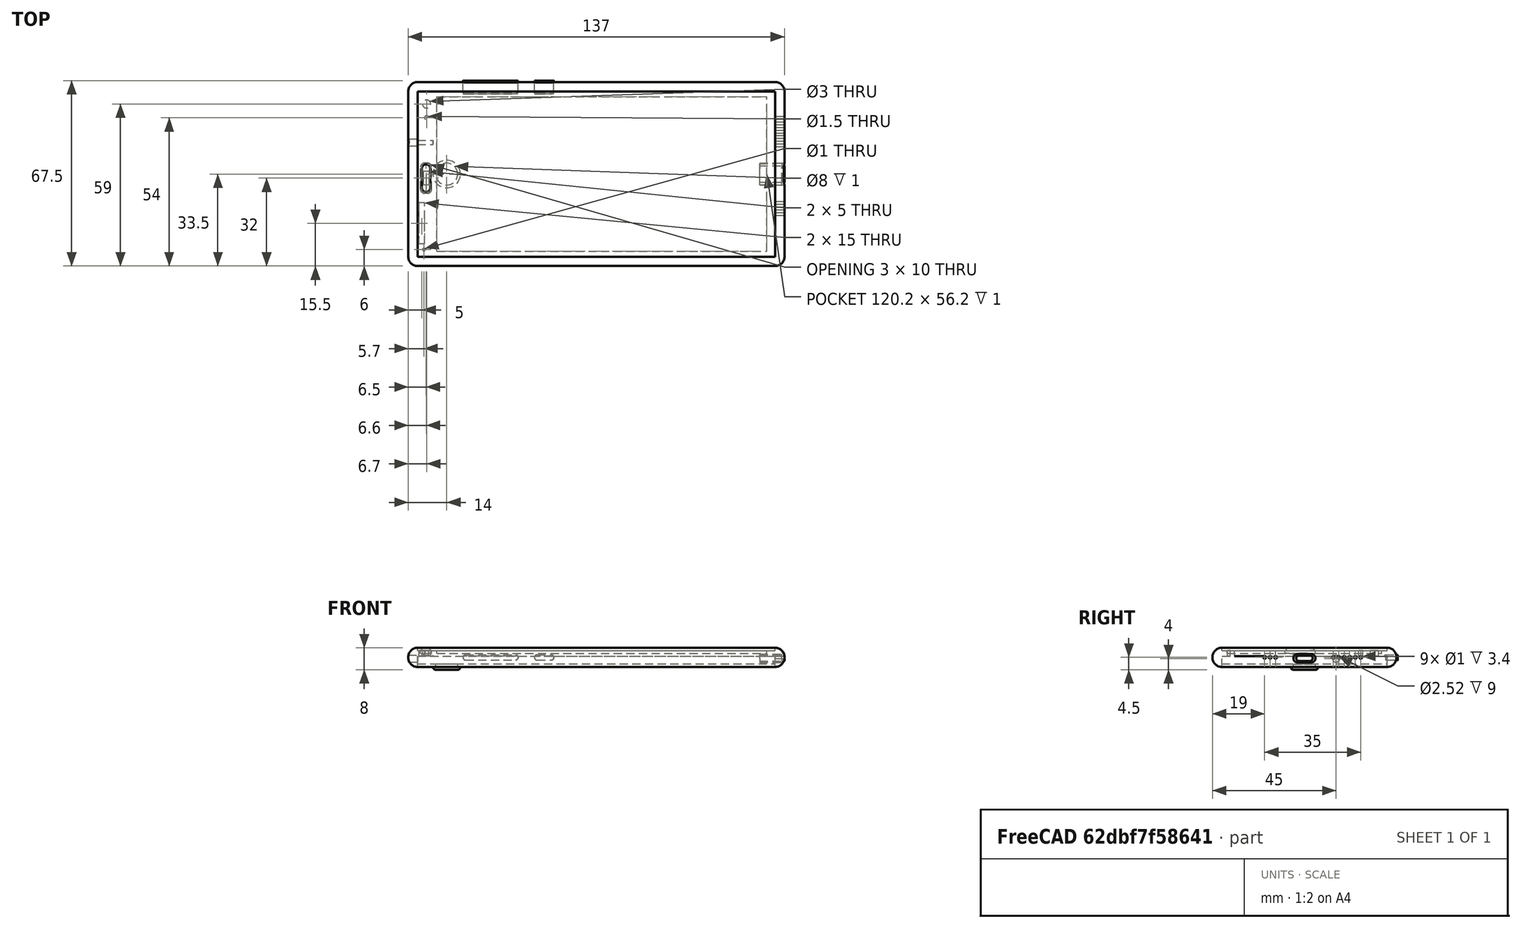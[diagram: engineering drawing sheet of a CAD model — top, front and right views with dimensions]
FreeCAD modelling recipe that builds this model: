
FCSTD DOCUMENT  (FreeCAD 0.15R4671 (Git))
Label: uCromy
License: All rights reserved
LicenseURL: http://es.wikipedia.org/wiki/Todos_los_derechos_reservados
objects: Part::Box×22, Part::Cylinder×19, Part::Cut×18, Part::Fillet×12, Part::MultiFuse×7
note: 78 computed .brp shape members not serialized (recipe doc carries the construction recipe); baked Part::Feature solids carry a one-line shape summary decoded from their .brp

FEATURE [Part::Box] Box  label="Cubo"
  Height = 7
  Length = 137
  Width = 67
FEATURE [Part::Fillet] Fillet
  Base = -> Box
  Edges = 12 edges r=3.4: [Edge1,Edge2,Edge3,Edge4,Edge5,Edge6,Edge7,Edge8,Edge9,Edge10,Edge11,Edge12]
FEATURE [Part::Box] Box001  label="Cubo001"
  Height = 10
  Length = 130.2
  Placement = pos=(3.4,3.4,-6) rot=(0,0,1;0rad)
  Width = 60.2
FEATURE [Part::Cut] Cut
  Base = -> Fillet
  Tool = -> Box001
FEATURE [Part::Box] Box002  label="Cubo002"
  Height = 6
  Length = 130.2
  Placement = pos=(3.4,3.4,5) rot=(0,0,1;0rad)
  Width = 60.2
FEATURE [Part::Cut] Cut001
  Base = -> Cut
  Tool = -> Box002
FEATURE [Part::Box] Box003  label="Marco Superior"
  Height = 1
  Length = 7
  Placement = pos=(3.4,3.4,5) rot=(0,0,1;0rad)
  Width = 60.2
FEATURE [Part::Box] Box004  label="Marco Inferior"
  Height = 1
  Length = 4
  Placement = pos=(130.6,3.4,5) rot=(0,0,1;0rad)
  Width = 60.6
FEATURE [Part::Box] Box005  label="Marco Izquierdo"
  Height = 1
  Length = 120.2
  Placement = pos=(10.4,3.4,5) rot=(0,0,1;0rad)
  Width = 2
FEATURE [Part::Box] Box006  label="Marco Derecho"
  Height = 1
  Length = 120.2
  Placement = pos=(10.4,61.6,5) rot=(0,0,1;0rad)
  Width = 2
FEATURE [Part::Box] Box007  label="Pantalla AMOLED"
  Height = 1
  Length = 120.2
  Placement = pos=(10.4,5.4,5) rot=(0,0,1;0rad)
  Width = 56.2
FEATURE [Part::MultiFuse] Fusion  label="Chasis sin perforar"
  Shapes = -> [Cut001,Box003,Box004,Box006,Box005]
FEATURE [Part::Box] Box008  label="Táctil sin perforar"
  Height = 1
  Length = 130.2
  Placement = pos=(3.4,3.4,6) rot=(0,0,1;0rad)
  Width = 60.2
FEATURE [Part::Box] Box009  label="Trasera sin perforar"
  Height = 1.2
  Length = 130.2
  Placement = pos=(3.4,3.4,0) rot=(0,0,1;0rad)
  Width = 60.2
FEATURE [Part::Cylinder] Cylinder  label="Cámara frontal"
  Angle = 360
  Height = 10
  Placement = pos=(6.7,59,0) rot=(0,0,1;0rad)
  Radius = 1.5
FEATURE [Part::Cylinder] Cylinder001  label="Cilindro001"
  Angle = 360
  Height = 10
  Placement = pos=(6.7,54,0) rot=(0,0,1;0rad)
  Radius = 0.75
FEATURE [Part::Cut] Cut002
  Base = -> Fusion
  Tool = -> Cylinder
FEATURE [Part::Cut] Cut003
  Base = -> Cut002
  Tool = -> Cylinder001
FEATURE [Part::Cut] Cut004  label="Tactil sin Altavoz"
  Base = -> Box008
  Tool = -> Cylinder001
FEATURE [Part::Cylinder] Cylinder002  label="Flash frontal"
  Angle = 360
  Height = 1
  Placement = pos=(6.7,54,6) rot=(0,0,1;0rad)
  Radius = 0.75
FEATURE [Part::Cylinder] Cylinder003  label="Cilindro003"
  Angle = 360
  Height = 10
  Placement = pos=(5.7,6,0) rot=(0,0,1;0rad)
  Radius = 0.5
FEATURE [Part::Cut] Cut005
  Base = -> Cut003
  Tool = -> Cylinder003
FEATURE [Part::Box] Box010  label="Cubo003"
  Height = 10
  Length = 2
  Placement = pos=(5.6,29.5,0) rot=(0,0,1;0rad)
  Width = 5
FEATURE [Part::Cut] Cut006
  Base = -> Cut005
  Tool = -> Box010
FEATURE [Part::Box] Box011  label="Cubo004"
  Height = 10
  Length = 3
  Placement = pos=(5,27,0) rot=(0,0,1;0rad)
  Width = 10
FEATURE [Part::Fillet] Fillet001
  Base = -> Box011
  Edges = 4 edges r=1.4: [Edge1,Edge3,Edge5,Edge7]
FEATURE [Part::Cut] Cut007  label="Táctil"
  Base = -> Cut004
  Tool = -> Fillet001
FEATURE [Part::Box] Box012  label="Cubo005"
  Height = 2
  Length = 4
  Placement = pos=(5,27,0) rot=(0,0,1;0rad)
  Width = 11
FEATURE [Part::Fillet] Fillet002
  Base = -> Box012
  Edges = 4 edges r=1.4: [Edge1,Edge3,Edge5,Edge7]
  Placement = pos=(-0.5,-0.5,5) rot=(0,0,1;0rad)
FEATURE [Part::Cut] Cut008
  Base = -> Cut006
  Tool = -> Fillet002
FEATURE [Part::Box] Box013  label="Cubo006"
  Height = 1
  Length = 4
  Placement = pos=(5,27,0) rot=(0,0,1;0rad)
  Width = 11
FEATURE [Part::Fillet] Fillet003  label="Embellecedor auricular"
  Base = -> Box013
  Edges = 4 edges r=1.4: [Edge1,Edge3,Edge5,Edge7]
  Placement = pos=(-0.5,-0.5,5) rot=(0,0,1;0rad)
FEATURE [Part::Box] Box014  label="Cubo007"
  Height = 10
  Length = 2
  Placement = pos=(4,8,0) rot=(0,0,1;0rad)
  Width = 15
FEATURE [Part::Cut] Cut009
  Base = -> Cut008
  Tool = -> Box014
FEATURE [Part::Cylinder] Cylinder004  label="Cilindro"
  Angle = 360
  Height = 2
  Placement = pos=(14,33.5,-1) rot=(0,0,1;0rad)
  Radius = 5
FEATURE [Part::Fillet] Fillet004
  Base = -> Cylinder004
  Edges = 1 edges r=1: [Edge3]
FEATURE [Part::Cylinder] Cylinder005  label="Cilindro004"
  Angle = 360
  Height = 3
  Placement = pos=(14,33.5,-2) rot=(0,0,1;0rad)
  Radius = 4
FEATURE [Part::Cylinder] Cylinder006  label="Cilindro005"
  Angle = 360
  Height = 1
  Placement = pos=(14,33.5,-1) rot=(0,0,1;0rad)
  Radius = 4
FEATURE [Part::MultiFuse] Fusion001
  Shapes = -> [Fillet004,Box009]
FEATURE [Part::Cut] Cut010
  Base = -> Fusion001
  Tool = -> Cylinder005
FEATURE [Part::Cylinder] Cylinder007  label="Cilindro006"
  Angle = 360
  Height = 3
  Placement = pos=(24,33.5,-2) rot=(0,0,1;0rad)
  Radius = 1.5
FEATURE [Part::Cut] Cut011
  Base = -> Cut010
  Tool = -> Cylinder007
FEATURE [Part::MultiFuse] Fusion002
  Shapes = -> [Cylinder006,Cut011]
FEATURE [Part::Cylinder] Cylinder008  label="Flash trasero"
  Angle = 360
  Height = 1
  Placement = pos=(24,33.5,0) rot=(0,0,1;0rad)
  Radius = 1.5
FEATURE [Part::Box] Box015  label="Cubo008"
  Height = 2
  Length = 7
  Placement = pos=(46,63,2.5) rot=(0,0,1;0rad)
  Width = 4.5
FEATURE [Part::Box] Box016  label="Cubo009"
  Height = 2
  Length = 20
  Placement = pos=(20,63,2.5) rot=(0,0,1;0rad)
  Width = 4.5
FEATURE [Part::Fillet] Fillet005
  Base = -> Box015
  Edges = 4 edges r=0.9: [Edge2,Edge4,Edge6,Edge8]
  Placement = pos=(0,-0.3,0) rot=(0,0,1;0rad)
FEATURE [Part::Fillet] Fillet006
  Base = -> Box016
  Edges = 4 edges r=0.9: [Edge2,Edge4,Edge6,Edge8]
  Placement = pos=(0,-0.3,0) rot=(0,0,1;0rad)
FEATURE [Part::MultiFuse] Fusion003  label="Tapa trasera"
  Shapes = -> [Fusion002,Cylinder008]
FEATURE [Part::Box] Box017  label="Cubo010"
  Height = 2
  Length = 20
  Placement = pos=(20,63,2.5) rot=(0,0,1;0rad)
  Width = 4.5
FEATURE [Part::Fillet] Fillet007  label="Volumen"
  Base = -> Box017
  Edges = 4 edges r=0.9: [Edge2,Edge4,Edge6,Edge8]
FEATURE [Part::Cut] Cut012
  Base = -> Cut009
  Tool = -> Fillet006
FEATURE [Part::Cut] Cut013
  Base = -> Cut012
  Tool = -> Fillet005
FEATURE [Part::Box] Box018  label="Cubo011"
  Height = 2
  Length = 7
  Placement = pos=(46,63,2.5) rot=(0,0,1;0rad)
  Width = 4.5
FEATURE [Part::Fillet] Fillet008  label="Encendido"
  Base = -> Box018
  Edges = 4 edges r=0.9: [Edge2,Edge4,Edge6,Edge8]
FEATURE [Part::Box] Box019  label="Cubo012"
  Height = 3
  Length = 10
  Placement = pos=(128,29.5,2) rot=(0,0,1;0rad)
  Width = 8
FEATURE [Part::Fillet] Fillet009
  Base = -> Box019
  Edges = 4 edges r=1.45: [Edge9,Edge10,Edge11,Edge12]
  Placement = pos=(0,0,-0.3) rot=(0,0,1;0rad)
FEATURE [Part::Cut] Cut014
  Base = -> Cut013
  Tool = -> Fillet009
FEATURE [Part::Box] Box021  label="Cubo014"
  Height = 3
  Length = 8
  Placement = pos=(128,29.5,2) rot=(0,0,1;0rad)
  Width = 8
FEATURE [Part::Fillet] Fillet010  label="USB-C 1"
  Base = -> Box021
  Edges = 4 edges r=1.45: [Edge9,Edge10,Edge11,Edge12]
  Placement = pos=(0,0,-0.3) rot=(0,0,1;0rad)
FEATURE [Part::Box] Box022  label="Cubo015"
  Height = 2
  Length = 9
  Placement = pos=(128,29.5,2) rot=(0,0,1;0rad)
  Width = 6
FEATURE [Part::Fillet] Fillet011  label="USB-C 2"
  Base = -> Box022
  Edges = 4 edges r=0.95: [Edge9,Edge10,Edge11,Edge12]
  Placement = pos=(0,1,0.2) rot=(0,0,1;0rad)
FEATURE [Part::Cylinder] Cylinder009  label="Cilindro007"
  Angle = 360
  Height = 10
  Placement = pos=(-1,45,3) rot=(0.57735,0.57735,0.57735;2.0944rad)
  Radius = 1.26
FEATURE [Part::Cut] Cut015
  Base = -> Cut014
  Tool = -> Cylinder009
FEATURE [Part::Cylinder] Cylinder010  label="Cilindro008"
  Angle = 360
  Height = 10
  Placement = pos=(129,48,3.5) rot=(0.57735,0.57735,0.57735;2.0944rad)
  Radius = 0.5
FEATURE [Part::Cylinder] Cylinder011  label="Cilindro009"
  Angle = 360
  Height = 10
  Placement = pos=(129,46,3.5) rot=(0.57735,0.57735,0.57735;2.0944rad)
  Radius = 0.5
FEATURE [Part::Cylinder] Cylinder012  label="Cilindro010"
  Angle = 360
  Height = 10
  Placement = pos=(129,44,3.5) rot=(0.57735,0.57735,0.57735;2.0944rad)
  Radius = 0.5
FEATURE [Part::Cylinder] Cylinder013  label="Cilindro011"
  Angle = 360
  Height = 10
  Placement = pos=(129,50,3.5) rot=(0.57735,0.57735,0.57735;2.0944rad)
  Radius = 0.5
FEATURE [Part::Cylinder] Cylinder014  label="Cilindro012"
  Angle = 360
  Height = 10
  Placement = pos=(129,52,3.5) rot=(0.57735,0.57735,0.57735;2.0944rad)
  Radius = 0.5
FEATURE [Part::Cylinder] Cylinder015  label="Cilindro013"
  Angle = 360
  Height = 10
  Placement = pos=(129,23,3.5) rot=(0.57735,0.57735,0.57735;2.0944rad)
  Radius = 0.5
FEATURE [Part::Cylinder] Cylinder016  label="Cilindro014"
  Angle = 360
  Height = 10
  Placement = pos=(129,21,3.5) rot=(0.57735,0.57735,0.57735;2.0944rad)
  Radius = 0.5
FEATURE [Part::Cylinder] Cylinder017  label="Cilindro015"
  Angle = 360
  Height = 10
  Placement = pos=(129,19,3.5) rot=(0.57735,0.57735,0.57735;2.0944rad)
  Radius = 0.5
FEATURE [Part::Cylinder] Cylinder018  label="Cilindro016"
  Angle = 360
  Height = 10
  Placement = pos=(129,54,3.5) rot=(0.57735,0.57735,0.57735;2.0944rad)
  Radius = 0.5
FEATURE [Part::MultiFuse] Fusion004  label="Cilindros altavoz"
  Shapes = -> [Cylinder014,Cylinder018,Cylinder013,Cylinder010,Cylinder011,Cylinder012]
FEATURE [Part::Cut] Cut016
  Base = -> Cut015
  Tool = -> Fusion004
FEATURE [Part::MultiFuse] Fusion005  label="Cilindros microfono"
  Shapes = -> [Cylinder015,Cylinder016,Cylinder017]
FEATURE [Part::Cut] Cut017  label="Chasis"
  Base = -> Cut016
  Tool = -> Fusion005
FEATURE [Part::MultiFuse] Fusion006  label="Pantalla Táctil"
  Shapes = -> [Cut007,Cylinder002]
